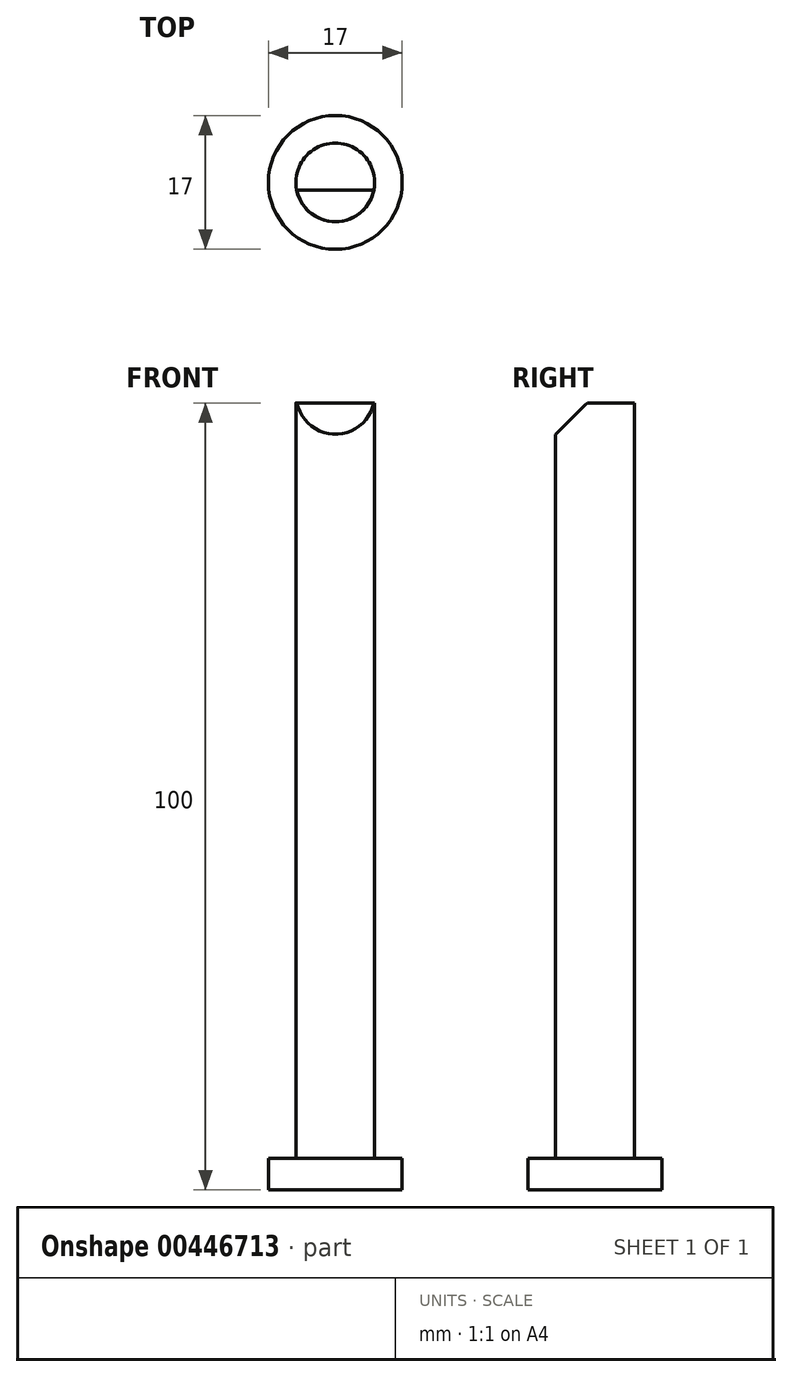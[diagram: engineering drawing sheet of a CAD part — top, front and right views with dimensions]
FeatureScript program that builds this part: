
annotation { "Feature Type Name" : "Feature", "Feature Type Description" : "" }
export const myFeature = defineFeature(function(context is Context, id is Id, definition is map)
    precondition{}
    {
        {
            var Q0;
            Q0=qCreatedBy(makeId("Top.planeOp"),FACE);
            var sketch = newSketch(context, id + "F0", { "sketchPlane" : qUnion([Q0])});
            skCircle(sketch, "E0", {"center": v(0, 0) * mm, "radius": 8.5 * mm});
            skSolve(sketch);
        }
        {
            var Q0;
            Q0=qSketchRegion(id+"F0",true);
            extrude(context, id + "F1", {"entities" : qUnion([Q0]), "depth" : 4 * mm});
        }
        {
            var Q0;
            Q0=qCreatedBy(makeId("Top.planeOp"),FACE);
            var sketch = newSketch(context, id + "F2", { "sketchPlane" : qUnion([Q0])});
            skCircle(sketch, "E1", {"center": v(0, 0) * mm, "radius": 5 * mm});
            skSolve(sketch);
        }
        {
            var Q0;
            Q0=qSketchRegion(id+"F2",true);
            extrude(context, id + "F3", {"entities" : qUnion([Q0]), "operationType" : NewBodyOperationType.ADD, "depth" : 100 * mm});
        }
        {
            var Q0;
            Q0=qCreatedBy(makeId("Right.planeOp"),FACE);
            var sketch = newSketch(context, id + "F4", { "sketchPlane" : qUnion([Q0])});
            skLineSegment(sketch, "E2", {"start": v(-5, 101) * mm, "end": v(-5, 96) * mm});
            skLineSegment(sketch, "E3", {"start": v(-5, 96) * mm, "end": v(0, 101) * mm});
            skLineSegment(sketch, "E4", {"start": v(0, 101) * mm, "end": v(-5, 101) * mm});
            skSolve(sketch);
        }
        {
            var Q0;
            Q0 = qSketchRegion(id + "F4", true);
            extrude(context, id + "F5", {"entities" : qUnion([Q0]), "operationType" : NewBodyOperationType.REMOVE, "depth" : 25 * mm, "hasSecondDirection" : true, "secondDirectionOppositeDirection" : true, "secondDirectionDepth" : 25 * mm});
        }
    });
